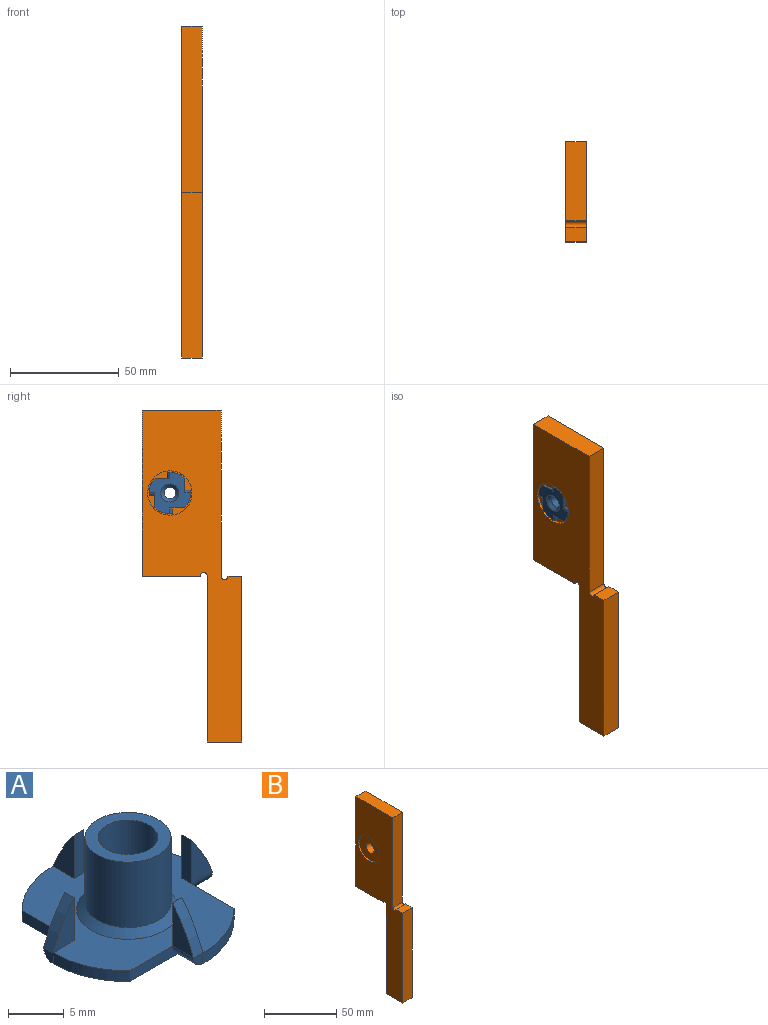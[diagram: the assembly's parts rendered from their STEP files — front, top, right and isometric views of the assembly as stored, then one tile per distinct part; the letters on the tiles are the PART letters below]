
ASSEMBLY  parts=2 mates=1
PART A: 39 faces, bbox 19.1x19.1x9.1 mm
  f0: cylinder r=9.53mm len=6.86mm, axis (0,0,-1), area 9.1mm2, adj f7,f10,f26,f28
  f1: cylinder r=16.73mm len=4.76mm, axis (0,-1,0), area 6.5mm2, adj f2,f3,f5,f6
  f2: plane 1.19x1.19mm, normal (1,0,0), area 1.1mm2, adj f1,f4,f27
  f3: plane 4.76x2.67mm, normal (0,-1,0), area 7.2mm2, adj f1,f4,f6
  f4: cylinder r=1.19mm len=2.67mm, axis (-1,0,0), area 5mm2, adj f2,f3,f7,f26
  f5: plane 4.76x2.67mm, normal (0,1,0), area 7.2mm2, adj f1,f6,f28
  f6: plane 4.76x1.19mm, normal (-1,0,0), area 5.7mm2, adj f1,f3,f5,f28
  f7: plane 6.61x1.19mm, normal (1,0,0), area 6.8mm2, adj f0,f4,f26,f28
  f8: cylinder r=9.53mm len=6.86mm, axis (0,0,-1), area 9.1mm2, adj f15,f18,f26,f28
  f9: cylinder r=16.73mm len=4.76mm, axis (-1,0,0), area 6.5mm2, adj f10,f11,f13,f14
  f10: plane 1.19x1.19mm, normal (0,-1,0), area 1.1mm2, adj f0,f9,f12
  f11: plane 4.76x2.67mm, normal (-1,0,0), area 7.2mm2, adj f9,f12,f14
  f12: cylinder r=1.19mm len=2.67mm, axis (0,1,0), area 5mm2, adj f10,f11,f15,f26
  f13: plane 4.76x2.67mm, normal (1,0,0), area 7.2mm2, adj f9,f14,f28
  f14: plane 4.76x1.19mm, normal (0,1,0), area 5.7mm2, adj f9,f11,f13,f28
  f15: plane 6.61x1.19mm, normal (0,-1,0), area 6.8mm2, adj f8,f12,f26,f28
  f16: cylinder r=9.53mm len=6.86mm, axis (0,0,-1), area 9.1mm2, adj f23,f26,f28,f34
  f17: cylinder r=16.73mm len=4.76mm, axis (0,1,0), area 6.5mm2, adj f18,f19,f21,f22
  f18: plane 1.19x1.19mm, normal (-1,0,0), area 1.1mm2, adj f8,f17,f20
  f19: plane 4.76x2.67mm, normal (0,1,0), area 7.2mm2, adj f17,f20,f22
  f20: cylinder r=1.19mm len=2.67mm, axis (1,0,0), area 5mm2, adj f18,f19,f23,f26
  f21: plane 4.76x2.67mm, normal (0,-1,0), area 7.2mm2, adj f17,f22,f28
  f22: plane 4.76x1.19mm, normal (1,0,0), area 5.7mm2, adj f17,f19,f21,f28
  f23: plane 6.61x1.19mm, normal (-1,0,0), area 6.8mm2, adj f16,f20,f26,f28
  f24: plane 4.76x2.67mm, normal (-1,0,0), area 7.2mm2, adj f28,f37,f38
  f25: cone r=2.68mm half-angle=45deg, axis (0,0,-1), area 44.3mm2, adj f26,f32
  f26: plane 19.05x19.05mm, normal (0,0,-1), area 182.6mm2, adj f0,f4,f7,f8,f12,f15,f16,f20
  f27: cylinder r=9.53mm len=6.86mm, axis (0,0,-1), area 9.1mm2, adj f2,f26,f28,f33
  f28: plane 19.05x19.05mm, normal (0,0,1), area 169mm2, adj f0,f5,f6,f7,f8,f13,f14,f15
  f29: cone r=4.64mm half-angle=45deg, axis (0,0,-1), area 28.8mm2, adj f28,f30
  f30: cylinder r=3.87mm len=7.75mm, axis (0,0,-1), area 174.9mm2, adj f29,f31
  f31: plane 7.75x7.75mm, normal (0,0,1), area 24.6mm2, adj f30,f32
  f32: cylinder r=2.68mm len=7.68mm, axis (0,0,-1), area 129.4mm2, adj f25,f31
  f33: plane 6.61x1.19mm, normal (0,1,0), area 6.8mm2, adj f26,f27,f28,f36
  f34: plane 1.19x1.19mm, normal (0,1,0), area 1.1mm2, adj f16,f36,f38
  f35: plane 4.76x2.67mm, normal (1,0,0), area 7.2mm2, adj f36,f37,f38
  f36: cylinder r=1.19mm len=2.67mm, axis (0,-1,0), area 5mm2, adj f26,f33,f34,f35
  f37: plane 4.76x1.19mm, normal (0,-1,0), area 5.7mm2, adj f24,f28,f35,f38
  f38: cylinder r=16.73mm len=4.76mm, axis (1,0,0), area 6.5mm2, adj f24,f34,f35,f37
PART B: 15 faces, bbox 9.5x45.7x152.4 mm
  f0: plane 9.53x6.35mm, normal (0,0,1), area 60.5mm2, adj f2,f3,f9,f13
  f1: plane 26.67x9.53mm, normal (0,0,-1), area 254mm2, adj f2,f6,f9,f14
  f2: plane 152.4x45.72mm, normal (-1,0,0), area 3635.5mm2, adj f0,f1,f3,f4,f5,f6,f7,f8
  f3: plane 76.2x9.53mm, normal (0,-1,0), area 725.8mm2, adj f0,f2,f4,f9
  f4: plane 15.88x9.53mm, normal (0,0,-1), area 151.2mm2, adj f2,f3,f5,f9
  f5: plane 76.2x9.53mm, normal (0,1,0), area 725.8mm2, adj f2,f4,f9,f14
  f6: plane 76.2x9.53mm, normal (0,1,0), area 725.8mm2, adj f1,f2,f7,f9
  f7: plane 36.2x9.53mm, normal (0,0,1), area 344.8mm2, adj f2,f6,f8,f9
  f8: plane 76.2x9.53mm, normal (0,-1,0), area 725.8mm2, adj f2,f7,f9,f13
  f9: plane 152.4x45.72mm, normal (1,0,0), area 3910.2mm2, adj f0,f1,f3,f4,f5,f6,f7,f8
  f10: cylinder r=3.98mm len=8.26mm, axis (-1,0,0), area 206.2mm2, adj f9,f11
  f11: plane 20.32x20.32mm, normal (-1,0,0), area 274.7mm2, adj f10,f12
  f12: cylinder r=10.16mm len=20.32mm, axis (-1,0,0), area 81.1mm2, adj f2,f11
  f13: cylinder r=1.59mm len=9.53mm, axis (-1,0,0), area 47.5mm2, adj f0,f2,f8,f9
  f14: cylinder r=1.59mm len=9.53mm, axis (-1,0,0), area 47.5mm2, adj f1,f2,f5,f9
PLACE A rot(axis=(-0.58,0.58,-0.58),120deg) t=(31.94,-49.31,-6.68)mm
PLACE B t=(31.87,-69.63,-130.5)mm
MATE fastened B.f10 <-> A.f0  axis (-1,0,0) through (33.14,-49.31,-6.68)mm
